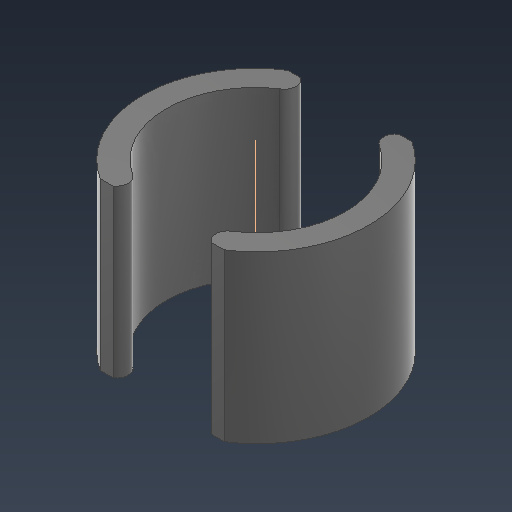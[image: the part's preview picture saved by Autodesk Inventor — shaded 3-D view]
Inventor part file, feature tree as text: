
AUTODESK INVENTOR PART (.ipt)
format: ipt  version: 2021 (Build 250183000, 183)  size: 149,504 bytes
history: native  units: mm
features: other x2, extrude x1, pattern_circular x1, sketch x1
ambient origin geometry x8: Origin, YZ Plane, XZ Plane, XY Plane, X Axis, Y Axis, Z Axis, Center Point
bodies: Body1 (feature_tree)
feature tree (5):
  other  "Imãs"
  other  "Sólido1"
  extrude  "Extrusão1"  Depth=8.5mm
  pattern_circular  "Padrão circular1"  [2 undecoded]
  sketch  "Esboço1"  dims[d21=0.2mm d22=0.2mm d23=0.2mm d24=0.2mm d28=1.0mm d29=5.0mm d30=90.0deg d31=1.0mm d32=1.0mm d33=1.0mm d34=8.5mm d35=0.0mm d36=20.0mm d37=360.0deg]
note: 2 required parameter values undecoded (feature->parameter linkage not recoverable at this tier; creation-order binding heuristic only, values carry confidence <= 0.55)
